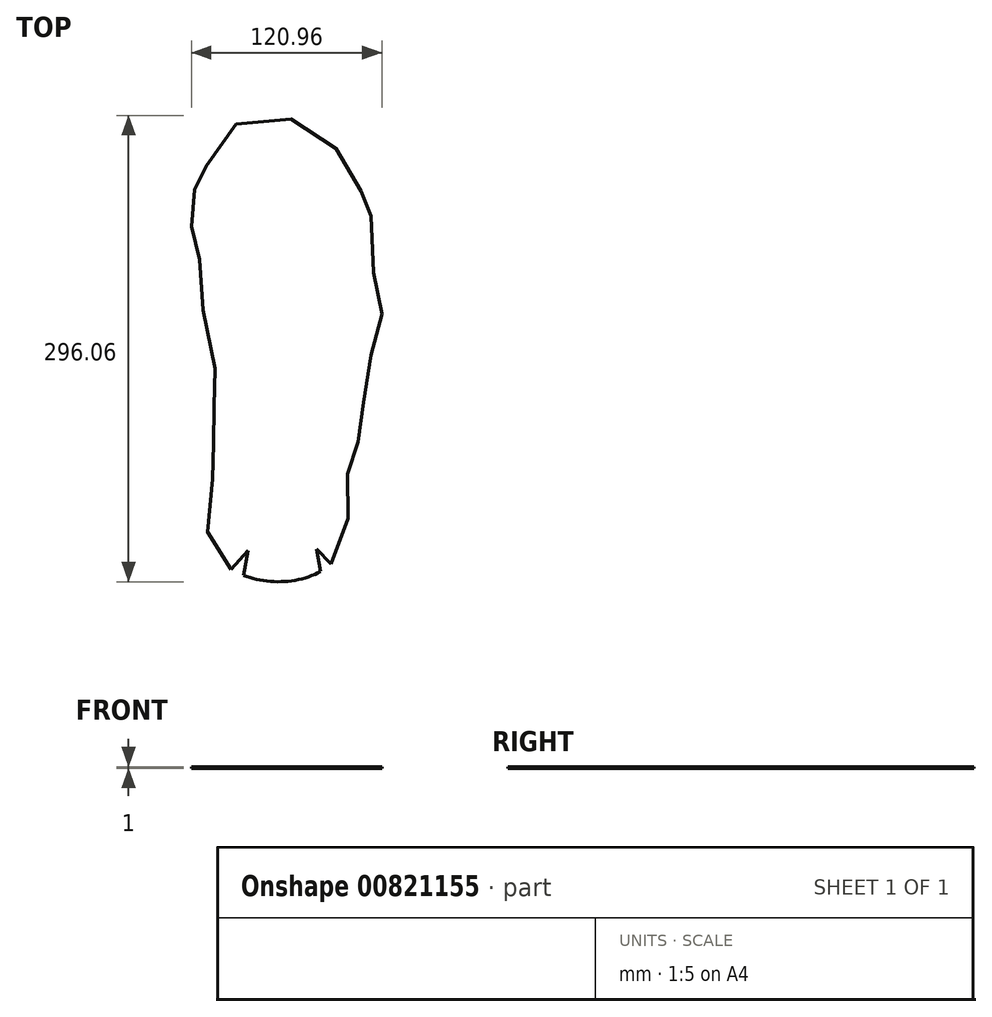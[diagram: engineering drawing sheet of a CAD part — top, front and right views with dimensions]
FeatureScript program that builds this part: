
annotation { "Feature Type Name" : "Feature", "Feature Type Description" : "" }
export const myFeature = defineFeature(function(context is Context, id is Id, definition is map)
    precondition{}
    {
        {
            var Q0;
            Q0=qCreatedBy(makeId("Top.planeOp"),FACE);
            var sketch = newSketch(context, id + "F0", { "sketchPlane" : qUnion([Q0])});
            skFitSpline(sketch, "E0", {"points": [v(-21.75, 140.48) * mm, v(20.32, 141.44) * mm, v(48.76, 115.45) * mm, v(60.49, 92.26) * mm, v(63.2, 87.47) * mm, v(65, 50.89) * mm, v(70.84, 21.13) * mm, v(69.6, 15.83) * mm, v(59.89, -27.9) * mm, v(58.9, -41.11) * mm, v(53.98, -67.28) * mm, v(49.15, -80.09) * mm, v(49.5, -105.45) * mm, v(39.82, -137.26) * mm, v(2.66, -149.93) * mm, v(-32.02, -136.3) * mm, v(-40.22, -108.75) * mm, v(-34.97, -72.79) * mm, v(-36.17, -60.5) * mm, v(-35.96, -41) * mm, v(-33.83, -24.18) * mm, v(-42.46, 19.5) * mm, v(-45.15, 56.09) * mm, v(-50.02, 71.84) * mm, v(-48.08, 88.33) * mm, v(-47.43, 106.12) * mm, v(-41.84, 112.58) * mm, v(-21.75, 140.48) * mm]});
            skLineSegment(sketch, "E1", {"start": v(31.95, -143.44) * mm, "end": v(29.29, -129.06) * mm});
            skLineSegment(sketch, "E2", {"start": v(29.29, -129.06) * mm, "end": v(38.45, -138.65) * mm});
            skLineSegment(sketch, "E3", {"start": v(-24.85, -142.07) * mm, "end": v(-14.26, -130.16) * mm});
            skLineSegment(sketch, "E4", {"start": v(-14.26, -130.16) * mm, "end": v(-16.97, -145.96) * mm});
            skSolve(sketch);
        }
        {
            var Q0;
            {var subQ1=sQuery(id+"F0.wireOp",EDGE,"E1");Q0=makeQuery(id+"F0.imprint","IMPRINT",FACE,{"disambiguationData":[TD([[makeQuery(id+"F0.imprint","IMPRINT",EDGE,{"derivedFrom":subQ1}),1.0]])]});}
            extrude(context, id + "F1", {"entities" : qUnion([Q0]), "depth" : 1 * mm, "offsetDistance" : 25 * mm});
        }
    });
